# Revit family: SFIP66_50W
name_source: partatom
category: Lighting Fixtures
revit_build: Autodesk Revit 2017 (Build: 20190507_1515(x64)
units: mm (PartAtom-declared; Revit-internal decimal feet)

## family parameters
Cut with Voids When Loaded = No
Host = Face
Light Source = No
OmniClass Number = 23.80.70.00
OmniClass Title = Lighting
Part Type = Normal
Room Calculation Point = No
Round Connector Dimension = Use Diameter
Shared = No

## types (1)
- 0048525 START FLOOD IP66 6KLM 830 ASYM
    100W_SYL = No
    150W_SYL = No
    200W_SYL = No
    50W_SYL = Yes
    Apparent Load = 50 VA
    Assembly Code = D5020200
    AssetType = Fixed
    AxisDepth_SYL = 49 mm
    AxisHeight_SYL = 71 mm
    AxisOffsetWingEnd_SYL = 15 mm  [stored 0.0492126 ft]
    ClassificationName = Uniclass2015
    ClassificationValue = EF_70_80
    Cost = 0 $
    Default Elevation = 1219 mm
    Description = Exterior LED Floodlight, comes complete with 1000mm flying lead and adjustable bracket, aluminium housing, clear glass diffuser, IP66, IK08, Class I, 3000K, Non-dimming, 6200lm, 50W, 124lm/W, CRI80, Asymmetrical Wide beam angle (65° x 120° imax@55°), 60000 hrs L70B50 lifetime, 314 x 240 x 63mm (LxWxD) dimensions, 2.5kg weight.
    DocumentationLiterature = http://www.sylvania-lighting.com
    ElectricShockClassification = Class I
    IfcExportAs = IfcLightFixtureType
    IfcExportType = IfcLightFixtureType
    ImpactProtectionIndex = IK08
    IngressProtection = IP66
    Keynote = 16500
    Lamp = LED
    LampColourRenderingIndex = 70
    LampColourTemperature = 3000 K
    LampMacAdamStep = 4
    LampNominalLuminous = 6200 lm
    LampsType = LED
    LengthIn_SYL = 210 mm  [stored 0.688976 ft]
    LuminousEfficacy = 124 lm/W
    Manufacturer = Feilo Sylvania
    ManufacturerName = Feilo Sylvania
    Material_1_SYL = Steel, Paint Finish, Dark Gray, Matte
    Material_2_SYL = <By Category>
    Material_3_SYL = <By Category>
    Material_4_SYL = <By Category>
    Model = Start Flood IP66 6KLM 830 ASYM
    ModelNumber = 0048525
    ModelReference = Start Flood IP66 6KLM 830 ASYM
    Name = Start Flood IP66 6KLM 830 ASYM
    NominalDepth = 240 mm  [stored 0.787402 ft]
    NominalHeight = 63 mm
    NominalLength = 314 mm
    PowerConsumption = 50 W
    PowerFactor = 0.95
    RadiusInBracket_SYL = 2 mm  [stored 0.00656168 ft]
    RadiusOutBracket_SYL = 5 mm  [stored 0.0164042 ft]
    ThicknessBracket_SYL = 3 mm  [stored 0.00984252 ft]
    Type Image = <None>
    TypeHead_SYL = START Flood IP66 50W luminaire : 0048525
    TypeName = Start Flood IP66 6KLM 830 ASYM
    URL = http://www.sylvania-lighting.com
    Voltage = 0 V
    Weight = 2.5 kg
    WidthBracket_SYL = 30 mm  [stored 0.0984252 ft]
    WingLength_SYL = 100 mm  [stored 0.328084 ft]
    WingRadius_SYL = 10 mm  [stored 0.0328084 ft]

note: [stored X ft] marks values corroborated as IEEE doubles in the binary element streams (Revit-internal decimal feet)

## geometry (parser evidence)
native form markers: Sweep x6
no freeform markers — native parametric forms only
